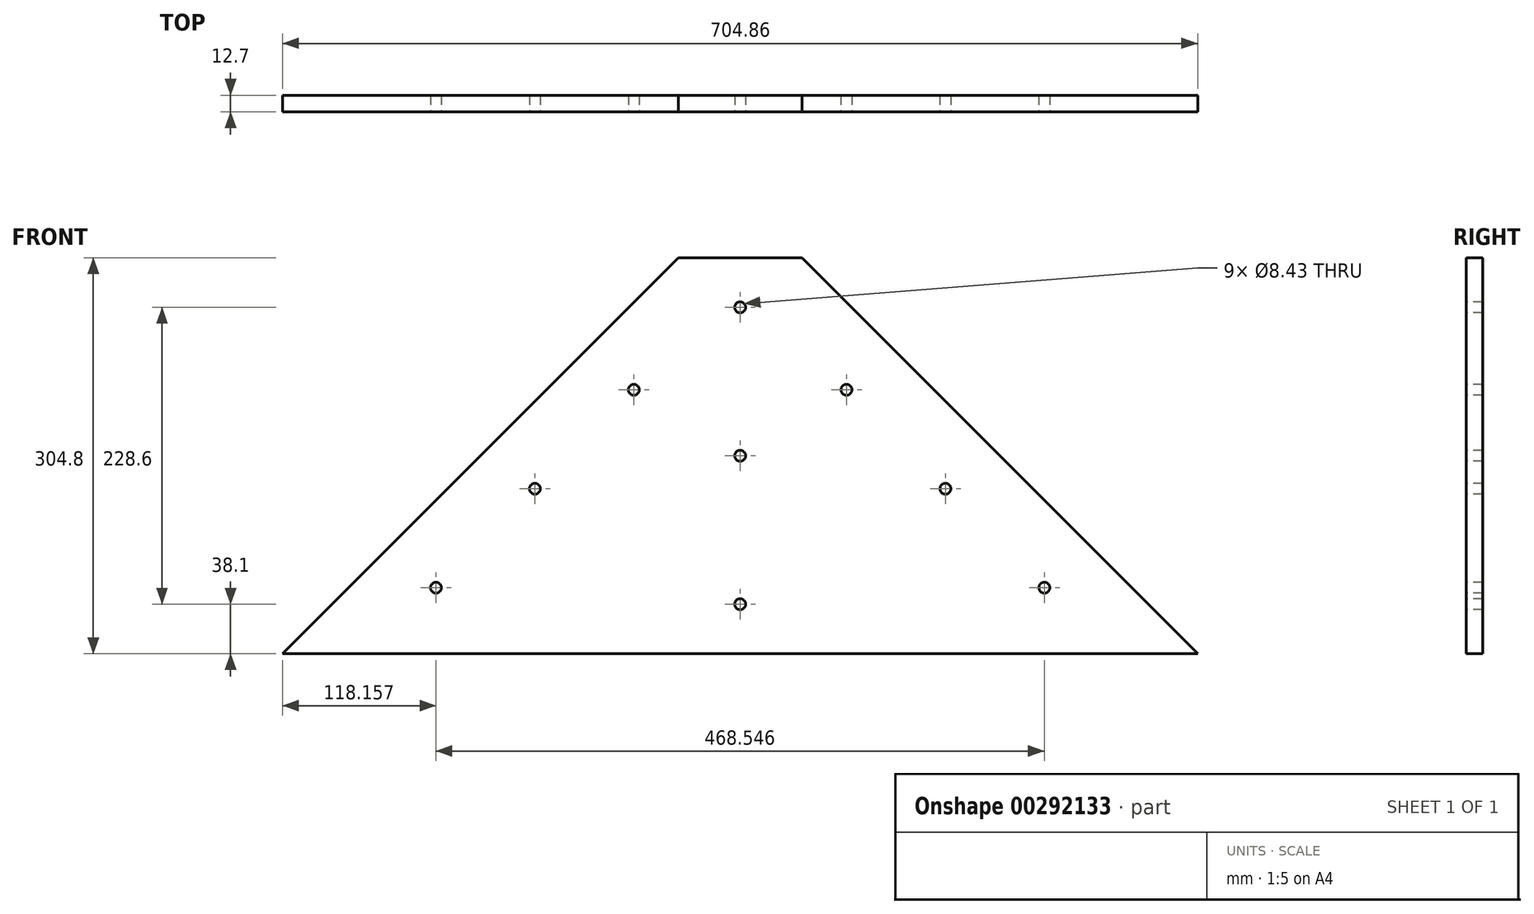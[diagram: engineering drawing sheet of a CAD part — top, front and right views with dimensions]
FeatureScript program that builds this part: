
annotation { "Feature Type Name" : "Feature", "Feature Type Description" : "" }
export const myFeature = defineFeature(function(context is Context, id is Id, definition is map)
    precondition{}
    {
        {
            var Q0;
            Q0=qCreatedBy(makeId("Front.planeOp"),FACE);
            var sketch = newSketch(context, id + "F0", { "sketchPlane" : qUnion([Q0])});
            skLineSegment(sketch, "E0", {"start": v(-47.63, 152.4) * mm, "end": v(47.62, 152.4) * mm});
            skLineSegment(sketch, "E1", {"start": v(47.62, 152.4) * mm, "end": v(352.43, -152.4) * mm});
            skLineSegment(sketch, "E2", {"start": v(352.43, -152.4) * mm, "end": v(-352.43, -152.4) * mm});
            skLineSegment(sketch, "E3", {"start": v(-352.43, -152.4) * mm, "end": v(-47.63, 152.4) * mm});
            skSolve(sketch);
        }
        {
            var Q0;
            Q0=makeQuery(id+"F0.imprint","IMPRINT",FACE,{"disambiguationData":[TD([[makeQuery(id+"F0.imprint","IMPRINT",EDGE,{"derivedFrom":sQuery(id+"F0.wireOp",EDGE,"E0")}),-1.0]])]});
            extrude(context, id + "F1", {"entities" : qUnion([Q0]), "depth" : 12.7 * mm});
        }
        {
            var Q0;
            Q0=makeQuery(id+"F1.opExtrude","CAP_FACE",FACE,{"disambiguationData":[OSD([sQuery(id+"F0.wireOp",EDGE,"E0"),sQuery(id+"F0.wireOp",EDGE,"E1"),sQuery(id+"F0.wireOp",EDGE,"E2"),sQuery(id+"F0.wireOp",EDGE,"E3")])],"isStart":false});
            var sketch = newSketch(context, id + "F2", { "sketchPlane" : qUnion([Q0])});
            skCircle(sketch, "E4", {"center": v(0, 114.3) * mm, "radius": 3.97 * mm});
            skCircle(sketch, "E5", {"center": v(0, 0) * mm, "radius": 3.97 * mm});
            skCircle(sketch, "E6", {"center": v(0, -114.3) * mm, "radius": 3.97 * mm});
            skCircle(sketch, "E7", {"center": v(-234.27, -101.6) * mm, "radius": 3.97 * mm});
            skCircle(sketch, "E8", {"center": v(-158.07, -25.4) * mm, "radius": 3.97 * mm});
            skCircle(sketch, "E9", {"center": v(-81.87, 50.8) * mm, "radius": 3.97 * mm});
            skCircle(sketch, "E10", {"center": v(234.27, -101.6) * mm, "radius": 3.97 * mm});
            skCircle(sketch, "E11", {"center": v(158.07, -25.4) * mm, "radius": 3.97 * mm});
            skCircle(sketch, "E12", {"center": v(81.87, 50.8) * mm, "radius": 3.97 * mm});
            skSolve(sketch);
        }
        {
            var Q0;
            Q0=sQuery(id+"F2.wireOp",VERTEX,"E4.center");
            var Q1;
            Q1=sQuery(id+"F2.wireOp",VERTEX,"E9.center");
            var Q2;
            Q2=sQuery(id+"F2.wireOp",VERTEX,"E8.center");
            var Q3;
            Q3=sQuery(id+"F2.wireOp",VERTEX,"E7.center");
            var Q4;
            Q4=sQuery(id+"F2.wireOp",VERTEX,"E6.center");
            var Q5;
            Q5=sQuery(id+"F2.wireOp",VERTEX,"E10.center");
            var Q6;
            Q6=sQuery(id+"F2.wireOp",VERTEX,"E11.center");
            var Q7;
            Q7=sQuery(id+"F2.wireOp",VERTEX,"E12.center");
            var Q8;
            Q8=sQuery(id+"F2.wireOp",VERTEX,"E5.center");
            var Q9;
            Q9=makeQuery(id+"F1.opExtrude","SWEPT_BODY",BODY,{"disambiguationData":[OSD([sQuery(id+"F0.wireOp",EDGE,"E0"),sQuery(id+"F0.wireOp",EDGE,"E1"),sQuery(id+"F0.wireOp",EDGE,"E2"),sQuery(id+"F0.wireOp",EDGE,"E3")])]});
            hole(context, id + "F3", {"style" : HoleStyle.SIMPLE, "endStyle" : HoleEndStyle.THROUGH, "standardTappedOrClearance" : lookupTablePath({ "standard" : "ANSI", "fit" : "Normal (ASME)", "size" : "5/16", "type" : "Clearance" }), "standardBlindInLast" : lookupTablePath({ "fit" : "Free", "standard" : "ANSI", "size" : "5/16", "type" : "Clearance" }), "holeDiameter" : 8.43 * mm, "tappedDepth" : 12.7 * mm, "tapClearance" : 3, "locations" : qUnion([Q0, Q1, Q2, Q3, Q4, Q5, Q6, Q7, Q8]), "scope" : qUnion([Q9])});
        }
    });
